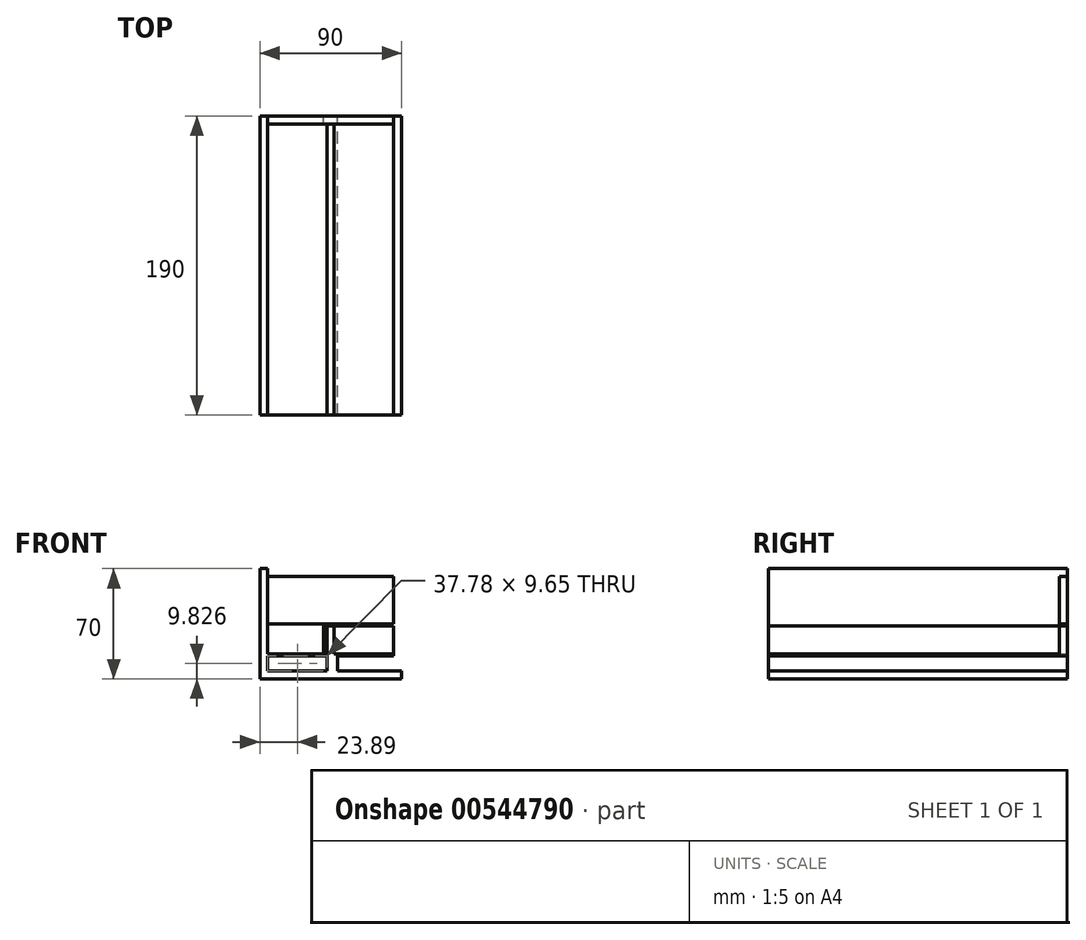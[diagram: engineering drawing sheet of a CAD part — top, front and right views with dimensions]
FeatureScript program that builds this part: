
annotation { "Feature Type Name" : "Feature", "Feature Type Description" : "" }
export const myFeature = defineFeature(function(context is Context, id is Id, definition is map)
    precondition{}
    {
        {
            var Q0;
            Q0=qCreatedBy(makeId("Front.planeOp"),FACE);
            var sketch = newSketch(context, id + "F0", { "sketchPlane" : qUnion([Q0])});
            skLineSegment(sketch, "E0.bottom", {"start": v(45, 35) * mm, "end": v(-45, 35) * mm});
            skLineSegment(sketch, "E0.top", {"start": v(45, -35) * mm, "end": v(-45, -35) * mm});
            skLineSegment(sketch, "E0.left", {"start": v(45, 35) * mm, "end": v(45, -35) * mm});
            skLineSegment(sketch, "E0.right", {"start": v(-45, 35) * mm, "end": v(-45, -35) * mm});
            skPoint(sketch, "E0.middle", {"position": v(0, 0) * mm});
            skLineSegment(sketch, "E1", {"start": v(-45, -35) * mm, "end": v(-45, -30) * mm});
            skLineSegment(sketch, "E2", {"start": v(-45, -30) * mm, "end": v(45, -30) * mm});
            skLineSegment(sketch, "E3", {"start": v(45, -30) * mm, "end": v(-45, -30) * mm});
            skLineSegment(sketch, "E4", {"start": v(-45, -30) * mm, "end": v(-40, -30) * mm});
            skLineSegment(sketch, "E5", {"start": v(-40, -30) * mm, "end": v(-40, 35) * mm});
            skLineSegment(sketch, "E6", {"start": v(-40, 35) * mm, "end": v(-40, 30) * mm});
            skLineSegment(sketch, "E7", {"start": v(-40, 30) * mm, "end": v(45, 30) * mm});
            skLineSegment(sketch, "E8", {"start": v(45, 30) * mm, "end": v(40, 30) * mm});
            skLineSegment(sketch, "E9", {"start": v(40, 30) * mm, "end": v(40, -30) * mm});
            skLineSegment(sketch, "E10", {"start": v(-40, -30) * mm, "end": v(-40, -20.35) * mm});
            skLineSegment(sketch, "E11", {"start": v(-40, -30) * mm, "end": v(-4.44, -30) * mm});
            skLineSegment(sketch, "E12", {"start": v(40, -30) * mm, "end": v(40, -20.35) * mm});
            skLineSegment(sketch, "E13", {"start": v(40, -20.35) * mm, "end": v(40, -30) * mm});
            skLineSegment(sketch, "E14", {"start": v(40, -30) * mm, "end": v(4.44, -30) * mm});
            skLineSegment(sketch, "E15", {"start": v(4.44, -30) * mm, "end": v(4.44, -20.35) * mm});
            skLineSegment(sketch, "E16", {"start": v(4.44, -20.35) * mm, "end": v(40, -20.35) * mm});
            skLineSegment(sketch, "E17", {"start": v(-4.44, -30) * mm, "end": v(-4.44, -20.35) * mm});
            skLineSegment(sketch, "E18", {"start": v(-4.44, -20.35) * mm, "end": v(-40, -20.35) * mm});
            skLineSegment(sketch, "E19", {"start": v(-40, -20.35) * mm, "end": v(-40, -19.08) * mm});
            skLineSegment(sketch, "E20", {"start": v(-40, -19.08) * mm, "end": v(-40, -1.3) * mm});
            skLineSegment(sketch, "E21", {"start": v(-40, -1.3) * mm, "end": v(-40, -0.03) * mm});
            skLineSegment(sketch, "E22", {"start": v(-40, -0.03) * mm, "end": v(-40, 30.45) * mm});
            skLineSegment(sketch, "E23", {"start": v(-40, -0.03) * mm, "end": v(40, -0.03) * mm});
            skLineSegment(sketch, "E24", {"start": v(-40, -1.3) * mm, "end": v(-4.44, -1.3) * mm});
            skLineSegment(sketch, "E25", {"start": v(-40, -19.08) * mm, "end": v(-4.44, -19.08) * mm});
            skLineSegment(sketch, "E26", {"start": v(-4.44, -19.08) * mm, "end": v(-4.44, -1.3) * mm});
            skLineSegment(sketch, "E27", {"start": v(40, -19.08) * mm, "end": v(4.44, -19.08) * mm});
            skLineSegment(sketch, "E28", {"start": v(4.44, -19.08) * mm, "end": v(4.44, -1.3) * mm});
            skLineSegment(sketch, "E29", {"start": v(4.44, -1.3) * mm, "end": v(40, -1.3) * mm});
            skLineSegment(sketch, "E30", {"start": v(-4.44, -19.08) * mm, "end": v(0, -19.08) * mm});
            skLineSegment(sketch, "E31.bottom", {"start": v(-4.44, -1.3) * mm, "end": v(-2.22, -1.3) * mm});
            skLineSegment(sketch, "E31.top", {"start": v(-4.44, -19.08) * mm, "end": v(-2.22, -19.08) * mm});
            skLineSegment(sketch, "E31.left", {"start": v(-4.44, -1.3) * mm, "end": v(-4.44, -19.08) * mm});
            skLineSegment(sketch, "E31.right", {"start": v(-2.22, -1.3) * mm, "end": v(-2.22, -19.08) * mm});
            skLineSegment(sketch, "E32.bottom", {"start": v(4.44, -1.3) * mm, "end": v(2.22, -1.3) * mm});
            skLineSegment(sketch, "E32.top", {"start": v(4.44, -19.08) * mm, "end": v(2.22, -19.08) * mm});
            skLineSegment(sketch, "E32.left", {"start": v(4.44, -1.3) * mm, "end": v(4.44, -19.08) * mm});
            skLineSegment(sketch, "E32.right", {"start": v(2.22, -1.3) * mm, "end": v(2.22, -19.08) * mm});
            skLineSegment(sketch, "E33.bottom", {"start": v(-4.44, -30) * mm, "end": v(-2.22, -30) * mm});
            skLineSegment(sketch, "E33.top", {"start": v(-4.44, -20.35) * mm, "end": v(-2.22, -20.35) * mm});
            skLineSegment(sketch, "E33.right", {"start": v(-2.22, -30) * mm, "end": v(-2.22, -20.35) * mm});
            skLineSegment(sketch, "E34.bottom", {"start": v(4.44, -20.35) * mm, "end": v(2.22, -20.35) * mm});
            skLineSegment(sketch, "E34.top", {"start": v(4.44, -30) * mm, "end": v(2.22, -30) * mm});
            skLineSegment(sketch, "E34.left", {"start": v(4.44, -20.35) * mm, "end": v(4.44, -30) * mm});
            skLineSegment(sketch, "E34.right", {"start": v(2.22, -20.35) * mm, "end": v(2.22, -30) * mm});
            skLineSegment(sketch, "E35", {"start": v(-2.22, -1.3) * mm, "end": v(2.22, -1.3) * mm});
            skLineSegment(sketch, "E36", {"start": v(-2.22, -20.35) * mm, "end": v(-2.22, -19.08) * mm});
            skLineSegment(sketch, "E37", {"start": v(2.22, -19.08) * mm, "end": v(2.22, -20.35) * mm});
            skSolve(sketch);
        }
        {
            var Q0;
            {var subQ1=sQuery(id+"F0.wireOp",EDGE,"E0.right");Q0=makeQuery(id+"F0.imprint","IMPRINT",FACE,{"disambiguationData":[TD([[makeQuery(id+"F0.imprint","IMPRINT",EDGE,{"derivedFrom":subQ1}),1.0]])]});}
            var Q1;
            {var subQ1=sQuery(id+"F0.wireOp",EDGE,"E6");Q1=makeQuery(id+"F0.imprint","IMPRINT",FACE,{"disambiguationData":[TD([[makeQuery(id+"F0.imprint","IMPRINT",EDGE,{"derivedFrom":subQ1}),1.0]])]});}
            var Q2;
            {var subQ0=sQuery(id+"F0.wireOp",EDGE,"E8");Q2=makeQuery(id+"F0.imprint","IMPRINT",FACE,{"disambiguationData":[TD([[makeQuery(id+"F0.imprint","IMPRINT",EDGE,{"derivedFrom":subQ0}),1.0]])]});}
            var Q3;
            {var subQ5=sQuery(id+"F0.wireOp",EDGE,"E0.top");Q3=makeQuery(id+"F0.imprint","IMPRINT",FACE,{"disambiguationData":[TD([[makeQuery(id+"F0.imprint","IMPRINT",EDGE,{"derivedFrom":subQ5}),-1.0]])]});}
            var Q4;
            {var subQ3=sQuery(id+"F0.wireOp",EDGE,"E15");Q4=makeQuery(id+"F0.imprint","IMPRINT",FACE,{"disambiguationData":[TD([[makeQuery(id+"F0.imprint","IMPRINT",EDGE,{"derivedFrom":subQ3}),1.0]])]});}
            var Q5;
            Q5=makeQuery(id+"F0.imprint","IMPRINT",FACE,{"disambiguationData":[TD([[makeQuery(id+"F0.imprint","IMPRINT",EDGE,{"derivedFrom":sQuery(id+"F0.wireOp",EDGE,"E21")}),-1.0]])]});
            var Q6;
            Q6=makeQuery(id+"F0.imprint","IMPRINT",FACE,{"disambiguationData":[TD([[makeQuery(id+"F0.imprint","IMPRINT",EDGE,{"derivedFrom":sQuery(id+"F0.wireOp",EDGE,"E31.right")}),1.0]])]});
            var Q7;
            Q7=makeQuery(id+"F0.imprint","IMPRINT",FACE,{"disambiguationData":[TD([[makeQuery(id+"F0.imprint","IMPRINT",EDGE,{"derivedFrom":sQuery(id+"F0.wireOp",EDGE,"E18")}),-1.0]])]});
            var Q8;
            {var subQ0=sQuery(id+"F0.wireOp",EDGE,"E16");Q8=makeQuery(id+"F0.imprint","IMPRINT",FACE,{"disambiguationData":[TD([[makeQuery(id+"F0.imprint","IMPRINT",EDGE,{"derivedFrom":subQ0}),1.0]])]});}
            extrude(context, id + "F1", {"entities" : qUnion([Q0, Q1, Q2, Q3, Q4, Q5, Q6, Q7, Q8]), "depth" : 190 * mm, "offsetDistance" : 25.4 * mm});
        }
        {
            var Q0;
            {var subQ0=sQuery(id+"F0.wireOp",EDGE,"E7");Q0=makeQuery(id+"F0.imprint","IMPRINT",FACE,{"disambiguationData":[TD([[makeQuery(id+"F0.imprint","IMPRINT",EDGE,{"derivedFrom":subQ0}),-1.0]])]});}
            var Q1;
            Q1=makeQuery(id+"F0.imprint","IMPRINT",FACE,{"disambiguationData":[TD([[makeQuery(id+"F0.imprint","IMPRINT",EDGE,{"derivedFrom":sQuery(id+"F0.wireOp",EDGE,"E20")}),-1.0]])]});
            var Q2;
            {var subQ0=sQuery(id+"F0.wireOp",EDGE,"E27");Q2=makeQuery(id+"F0.imprint","IMPRINT",FACE,{"disambiguationData":[TD([[makeQuery(id+"F0.imprint","IMPRINT",EDGE,{"derivedFrom":subQ0}),-1.0]])]});}
            var Q3;
            Q3=makeQuery(id+"F0.imprint","IMPRINT",FACE,{"disambiguationData":[TD([[makeQuery(id+"F0.imprint","IMPRINT",EDGE,{"derivedFrom":sQuery(id+"F0.wireOp",EDGE,"E13")}),-1.0]])]});
            var Q4;
            Q4=makeQuery(id+"F0.imprint","IMPRINT",FACE,{"disambiguationData":[TD([[makeQuery(id+"F0.imprint","IMPRINT",EDGE,{"derivedFrom":sQuery(id+"F0.wireOp",EDGE,"E10")}),-1.0]])]});
            var Q5;
            Q5=makeQuery(id+"F0.imprint","IMPRINT",FACE,{"disambiguationData":[TD([[makeQuery(id+"F0.imprint","IMPRINT",EDGE,{"derivedFrom":sQuery(id+"F0.wireOp",EDGE,"E31.bottom")}),-1.0]])]});
            var Q6;
            Q6=makeQuery(id+"F0.imprint","IMPRINT",FACE,{"disambiguationData":[TD([[makeQuery(id+"F0.imprint","IMPRINT",EDGE,{"derivedFrom":sQuery(id+"F0.wireOp",EDGE,"E33.bottom")}),1.0]])]});
            var Q7;
            Q7=makeQuery(id+"F0.imprint","IMPRINT",FACE,{"disambiguationData":[TD([[makeQuery(id+"F0.imprint","IMPRINT",EDGE,{"derivedFrom":sQuery(id+"F0.wireOp",EDGE,"E34.bottom")}),1.0]])]});
            var Q8;
            Q8=makeQuery(id+"F0.imprint","IMPRINT",FACE,{"disambiguationData":[TD([[makeQuery(id+"F0.imprint","IMPRINT",EDGE,{"derivedFrom":sQuery(id+"F0.wireOp",EDGE,"E32.bottom")}),1.0]])]});
            extrude(context, id + "F2", {"entities" : qUnion([Q0, Q1, Q2, Q3, Q4, Q5, Q6, Q7, Q8]), "operationType" : NewBodyOperationType.ADD, "depth" : 5 * mm, "offsetDistance" : 25.4 * mm});
        }
    });
